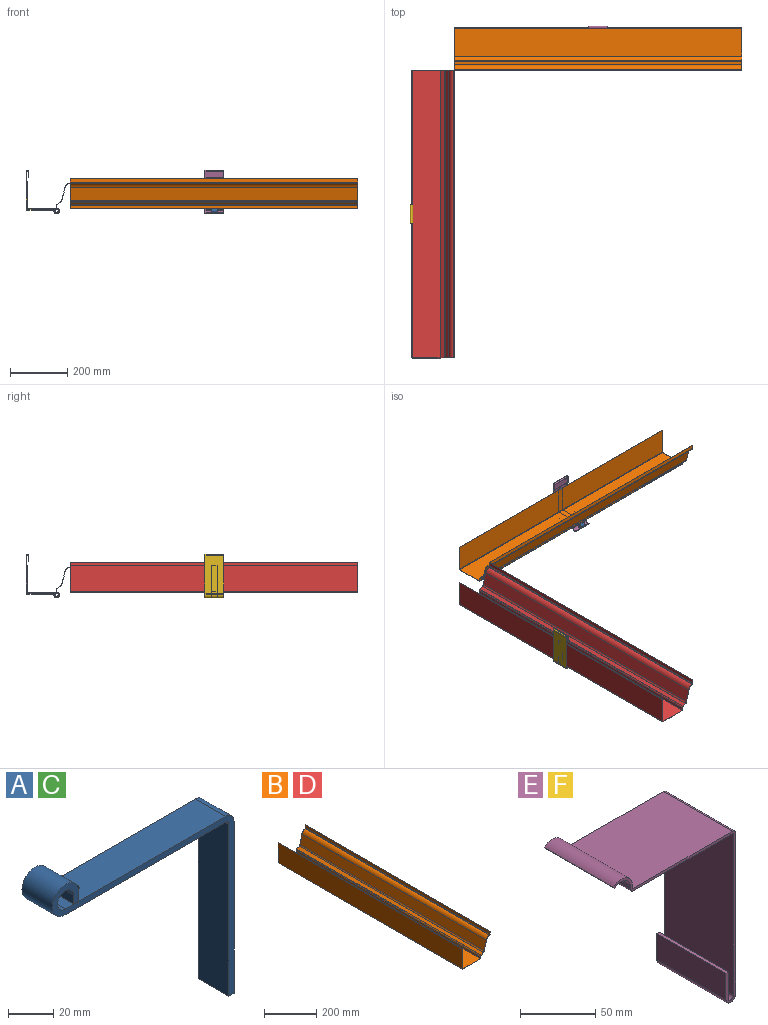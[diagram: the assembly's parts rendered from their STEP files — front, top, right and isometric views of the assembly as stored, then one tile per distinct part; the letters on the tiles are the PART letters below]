
ASSEMBLY  parts=6 mates=4
PART A: 15 faces, bbox 113.4x19x111.4 mm
  f0: plane 19x4.8mm, normal (-1,0,0), area 91.2mm2, adj f1,f11,f12,f13
  f1: plane 19x3.2mm, normal (0,0,-1), area 60.8mm2, adj f0,f2,f12,f13
  f2: plane 19x4.8mm, normal (1,0,0), area 91.2mm2, adj f1,f3,f12,f13
  f3: cylinder r=8.2mm len=19mm, axis (0,1,0), area 734.2mm2, adj f2,f4,f12,f13
  f4: plane 100x19mm, normal (0,0,-1), area 1880.4mm2, adj f3,f5,f12,f13,f14
  f5: cylinder r=2mm len=19mm, axis (0,1,0), area 59.7mm2, adj f4,f6,f12,f13
  f6: plane 92.98x19mm, normal (-1,0,0), area 1766.6mm2, adj f5,f7,f12,f13
  f7: plane 19x3.2mm, normal (0,0,-1), area 60.8mm2, adj f6,f8,f12,f13
  f8: plane 92.98x19mm, normal (1,0,0), area 1766.6mm2, adj f7,f9,f12,f13
  f9: cylinder r=5.2mm len=19mm, axis (0,1,0), area 155.2mm2, adj f8,f10,f12,f13
  f10: plane 100x19mm, normal (0,0,1), area 1880.4mm2, adj f9,f11,f12,f13,f14
  f11: cylinder r=5mm len=19mm, axis (0,1,0), area 447.7mm2, adj f0,f10,f12,f13
  f12: plane 113.4x111.38mm, normal (0,-1,0), area 750.5mm2, adj f0,f1,f2,f3,f4,f5,f6,f7
  f13: plane 113.4x111.38mm, normal (0,1,0), area 750.5mm2, adj f0,f1,f2,f3,f4,f5,f6,f7
  f14: cylinder r=2.5mm len=5mm, axis (0,0,-1), area 50.3mm2, adj f4,f10
PART B: 26 faces, bbox 150x1000x105 mm
  f0: plane 1000x1mm, normal (0,0,1), area 1000mm2, adj f1,f23,f24,f25
  f1: plane 1000x13.63mm, normal (-1,0,0), area 13625mm2, adj f0,f2,f24,f25
  f2: cylinder r=4mm len=1000mm, axis (0,1,0), area 4582.8mm2, adj f1,f3,f24,f25
  f3: cylinder r=21mm len=1000mm, axis (0,1,0), area 24408.7mm2, adj f2,f4,f24,f25
  f4: plane 1000x44.29mm, normal (-0.97,0,0.25), area 45694.1mm2, adj f3,f5,f24,f25
  f5: cylinder r=8.68mm len=1000mm, axis (0,1,0), area 6853.6mm2, adj f4,f6,f24,f25
  f6: plane 1000x12.46mm, normal (-0.51,0,0.86), area 14471.5mm2, adj f5,f7,f24,f25
  f7: cylinder r=6mm len=1000mm, axis (0,1,0), area 6225.7mm2, adj f6,f8,f24,f25
  f8: plane 1000x9mm, normal (-1,0,0), area 9000mm2, adj f7,f9,f24,f25
  f9: plane 1000x97mm, normal (0,0,1), area 97000mm2, adj f8,f10,f24,f25
  f10: cylinder r=1mm len=1000mm, axis (0,1,0), area 1570.8mm2, adj f9,f11,f24,f25
  f11: plane 1000x93mm, normal (1,0,0), area 93000mm2, adj f10,f12,f24,f25
  f12: plane 1000x1mm, normal (0,0,1), area 1000mm2, adj f11,f13,f24,f25
  f13: plane 1000x93mm, normal (-1,0,0), area 93000mm2, adj f12,f14,f24,f25
  f14: cylinder r=2mm len=1000mm, axis (0,1,0), area 3141.6mm2, adj f13,f15,f24,f25
  f15: plane 1000x98mm, normal (0,0,-1), area 98000mm2, adj f14,f16,f24,f25
  f16: plane 1000x10mm, normal (1,0,0), area 10000mm2, adj f15,f17,f24,f25
  f17: cylinder r=5mm len=1000mm, axis (0,1,0), area 5188.1mm2, adj f16,f18,f24,f25
  f18: plane 1000x12.46mm, normal (0.51,0,-0.86), area 14471.5mm2, adj f17,f19,f24,f25
  f19: cylinder r=9.68mm len=1000mm, axis (0,1,0), area 7643mm2, adj f18,f20,f24,f25
  f20: plane 1000x44.29mm, normal (0.97,0,-0.25), area 45694.1mm2, adj f19,f21,f24,f25
  f21: cylinder r=20mm len=1000mm, axis (0,1,0), area 23371.1mm2, adj f20,f22,f24,f25
  f22: cylinder r=5mm len=1000mm, axis (0,1,0), area 5909.4mm2, adj f21,f23,f24,f25
  f23: plane 1000x13.59mm, normal (1,0,0), area 13585.8mm2, adj f0,f22,f24,f25
  f24: plane 150x105mm, normal (0,-1,0), area 318.2mm2, adj f0,f1,f2,f3,f4,f5,f6,f7
  f25: plane 150x105mm, normal (0,1,0), area 318.2mm2, adj f0,f1,f2,f3,f4,f5,f6,f7
PART C: same geometry as A
PART D: same geometry as B
PART E: 20 faces, bbox 114.9x65x152 mm
  f0: plane 65x1.7mm, normal (-1,0,0), area 110.5mm2, adj f1,f17,f18,f19
  f1: cylinder r=3mm len=65mm, axis (0,1,0), area 306.3mm2, adj f0,f2,f18,f19
  f2: plane 93x65mm, normal (0,0,-1), area 6045mm2, adj f1,f3,f18,f19
  f3: cylinder r=1mm len=65mm, axis (0,1,0), area 102.1mm2, adj f2,f4,f18,f19
  f4: plane 131.3x65mm, normal (-1,0,0), area 8534.5mm2, adj f3,f5,f18,f19
  f5: cylinder r=2.5mm len=65mm, axis (0,1,0), area 510.5mm2, adj f4,f6,f18,f19
  f6: plane 65x21.5mm, normal (1,0,0), area 1397.5mm2, adj f5,f7,f18,f19
  f7: plane 65x2mm, normal (0,0,1), area 130mm2, adj f6,f8,f18,f19
  f8: plane 65x21.5mm, normal (-1,0,0), area 1397.5mm2, adj f7,f9,f18,f19
  f9: cylinder r=4.5mm len=65mm, axis (0,1,0), area 918.9mm2, adj f8,f10,f18,f19
  f10: plane 131.3x65mm, normal (1,0,0), area 8534.5mm2, adj f9,f11,f18,f19
  f11: cylinder r=3mm len=65mm, axis (0,1,0), area 306.3mm2, adj f10,f12,f18,f19
  f12: plane 93x65mm, normal (0,0,1), area 6045mm2, adj f11,f13,f18,f19
  f13: cylinder r=1mm len=65mm, axis (0,1,0), area 102.1mm2, adj f12,f14,f18,f19
  f14: plane 65x1.7mm, normal (1,0,0), area 110.5mm2, adj f13,f15,f18,f19
  f15: cylinder r=10.5mm len=65mm, axis (0,1,0), area 1608.1mm2, adj f14,f16,f18,f19
  f16: plane 65x1.41mm, normal (-0.71,0,-0.71), area 130mm2, adj f15,f17,f18,f19
  f17: cylinder r=8.5mm len=65mm, axis (0,1,0), area 1301.8mm2, adj f0,f16,f18,f19
  f18: plane 152x114.92mm, normal (0,-1,0), area 574.3mm2, adj f0,f1,f2,f3,f4,f5,f6,f7
  f19: plane 152x114.92mm, normal (0,1,0), area 574.3mm2, adj f0,f1,f2,f3,f4,f5,f6,f7
PART F: same geometry as E
PLACE A rot(axis=(-0.71,-0.71,0),180deg) t=(287.71,342.09,-97.72)mm
PLACE B rot(axis=(0,0,-1),90deg) t=(778.21,369.09,-37.04)mm
PLACE C rot(axis=(0,-1,0),180deg) t=(-269.79,-196.41,-97.72)mm
PLACE D t=(-296.79,294.09,-37.04)mm
PLACE E rot(axis=(-0.71,-0.71,0),180deg) t=(310.71,357.72,-90.01)mm fixed
PLACE F rot(axis=(0,-1,0),180deg) t=(-285.42,-173.41,-90.01)mm fixed
MATE fastened D.f13 <-> C.f6  axis (-1,0,0) through (-371.79,-205.91,5.46)mm
MATE revolute C.f3 <-> F.f15  axis (0,1,0) through (-269.79,-205.91,-97.72)mm
MATE fastened B.f13 <-> A.f6  axis (0,1,0) through (278.21,444.09,5.46)mm
MATE revolute A.f3 <-> E.f15  axis (1,0,0) through (278.21,342.09,-97.72)mm
